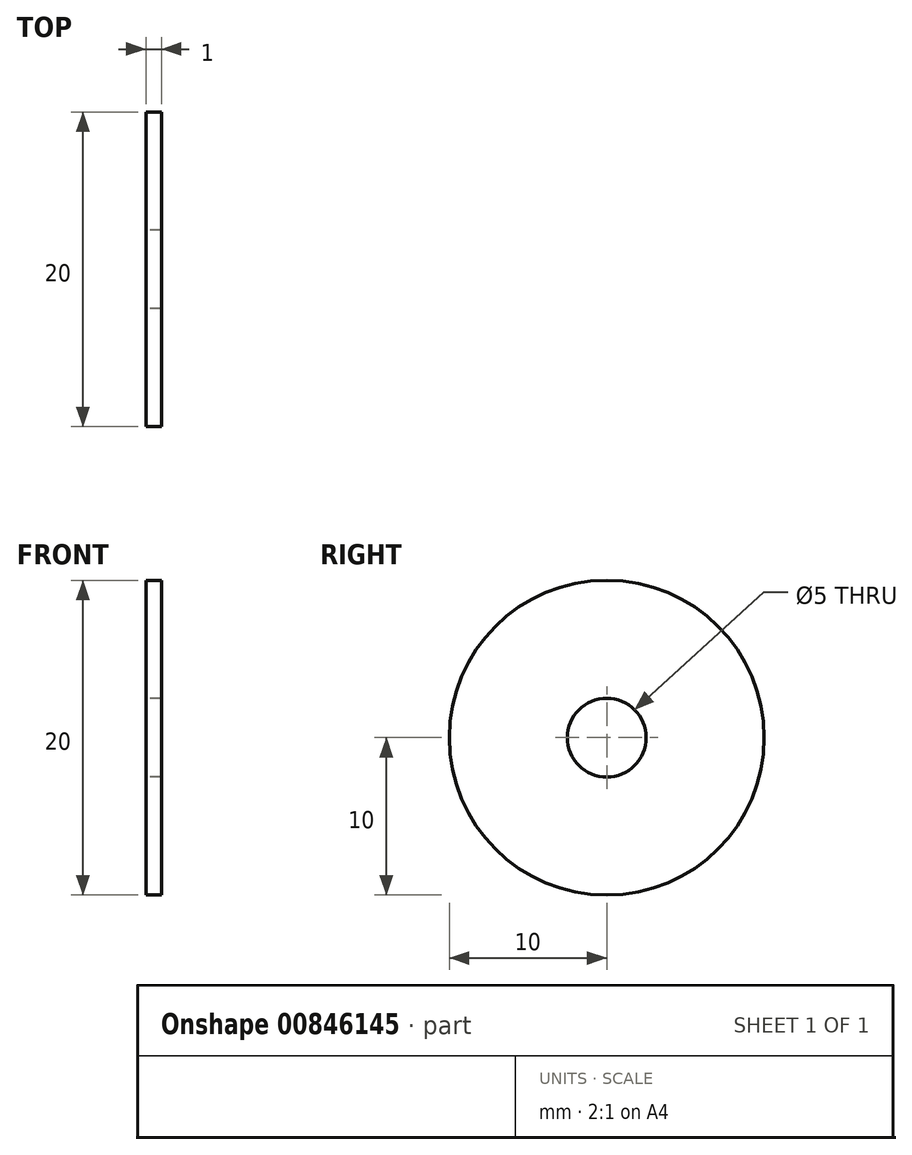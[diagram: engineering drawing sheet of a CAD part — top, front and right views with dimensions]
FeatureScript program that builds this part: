
annotation { "Feature Type Name" : "Feature", "Feature Type Description" : "" }
export const myFeature = defineFeature(function(context is Context, id is Id, definition is map)
    precondition{}
    {
        {
            var Q0;
            Q0=qCreatedBy(makeId("Right.planeOp"),FACE);
            var sketch = newSketch(context, id + "F0", { "sketchPlane" : qUnion([Q0])});
            skCircle(sketch, "E0", {"center": v(0, 0) * mm, "radius": 10 * mm});
            skCircle(sketch, "E1", {"center": v(0, 0) * mm, "radius": 2.5 * mm});
            skSolve(sketch);
        }
        {
            var Q0;
            Q0=makeQuery(id+"F0.imprint","IMPRINT",FACE,{"disambiguationData":[TD([[makeQuery(id+"F0.imprint","IMPRINT",EDGE,{"derivedFrom":sQuery(id+"F0.wireOp",EDGE,"E0")}),1.0]])]});
            extrude(context, id + "F1", {"entities" : qUnion([Q0]), "depth" : 1 * mm, "offsetDistance" : 25 * mm});
        }
    });
